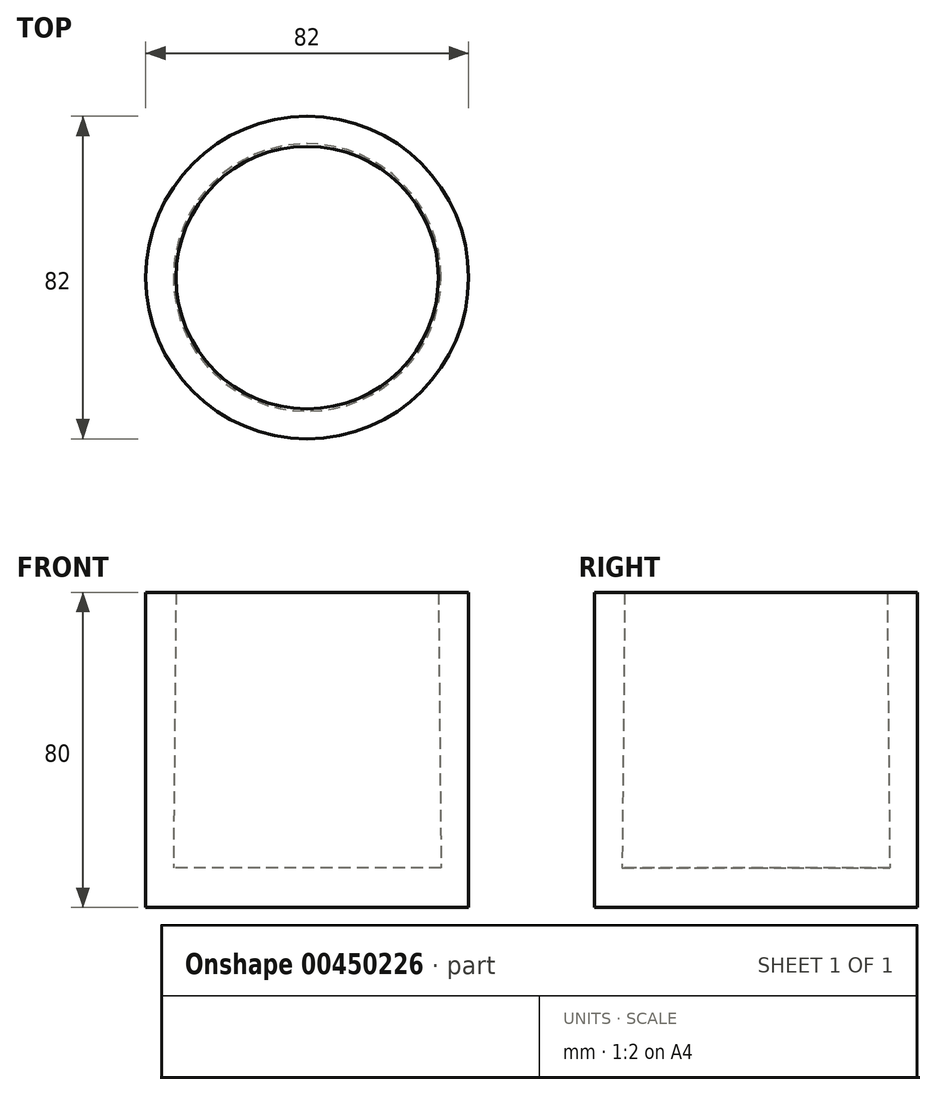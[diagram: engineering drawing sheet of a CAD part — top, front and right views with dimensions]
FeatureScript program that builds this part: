
annotation { "Feature Type Name" : "Feature", "Feature Type Description" : "" }
export const myFeature = defineFeature(function(context is Context, id is Id, definition is map)
    precondition{}
    {
        {
            var Q0;
            Q0=qCreatedBy(makeId("Right.planeOp"),FACE);
            var sketch = newSketch(context, id + "F0", { "sketchPlane" : qUnion([Q0])});
            skLineSegment(sketch, "E0", {"start": v(0, 0) * mm, "end": v(-34, 0) * mm});
            skLineSegment(sketch, "E1", {"start": v(-34, 0) * mm, "end": v(-34, 10) * mm});
            skLineSegment(sketch, "E2", {"start": v(-34, 10) * mm, "end": v(0, 10) * mm});
            skLineSegment(sketch, "E3", {"start": v(0, 10) * mm, "end": v(0, 0) * mm});
            skLineSegment(sketch, "E4", {"start": v(-34, 0) * mm, "end": v(-41, 0) * mm});
            skLineSegment(sketch, "E5", {"start": v(-41, 0) * mm, "end": v(-41, 10) * mm});
            skLineSegment(sketch, "E6", {"start": v(-41, 10) * mm, "end": v(-34, 10) * mm});
            skLineSegment(sketch, "E7", {"start": v(-41, 10) * mm, "end": v(-41, 80) * mm});
            skLineSegment(sketch, "E8", {"start": v(-41, 80) * mm, "end": v(-33.34, 80) * mm});
            skLineSegment(sketch, "E9", {"start": v(-33.34, 80) * mm, "end": v(-34, 10) * mm});
            skSolve(sketch);
        }
        {
            var Q0;
            Q0 = qSketchRegion(id + "F0", true);
            var Q1;
            Q1=sQuery(id+"F0.wireOp",EDGE,"E3");
            revolve(context, id + "F1", {"entities" : qUnion([Q0]), "axis" : qUnion([Q1]), "revolveType" : RevolveType.FULL});
        }
    });
